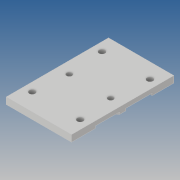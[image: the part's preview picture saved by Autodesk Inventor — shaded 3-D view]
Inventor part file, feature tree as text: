
AUTODESK INVENTOR PART (.ipt)
format: ipt  version: 2019 (Build 230136000, 136)  size: 137,216 bytes
history: native  units: mm
features: sketch x4, extrude x2, hole x2, chamfer x1, projected_geometry x1
ambient origin geometry x8: Origin, YZ Plane, XZ Plane, XY Plane, X Axis, Y Axis, Z Axis, Center Point
bodies: Solide1 (feature_tree)
feature tree (10):
  extrude  "Extrusion1"  Depth=60.0mm
  hole  "Perçage1"  [1 undecoded]
  hole  "Perçage2"  [1 undecoded]
  extrude  "Extrusion2"  Depth=16.0mm
  chamfer  "Chanfrein1"  Distance=14.0mm
  sketch  "Esquisse1"
  sketch  "Esquisse2"
  sketch  "Esquisse4"
  sketch  "Esquisse5"
  projected_geometry  "Boucle projetée1"
note: 2 required parameter values undecoded (feature->parameter linkage not recoverable at this tier; creation-order binding heuristic only, values carry confidence <= 0.55)
